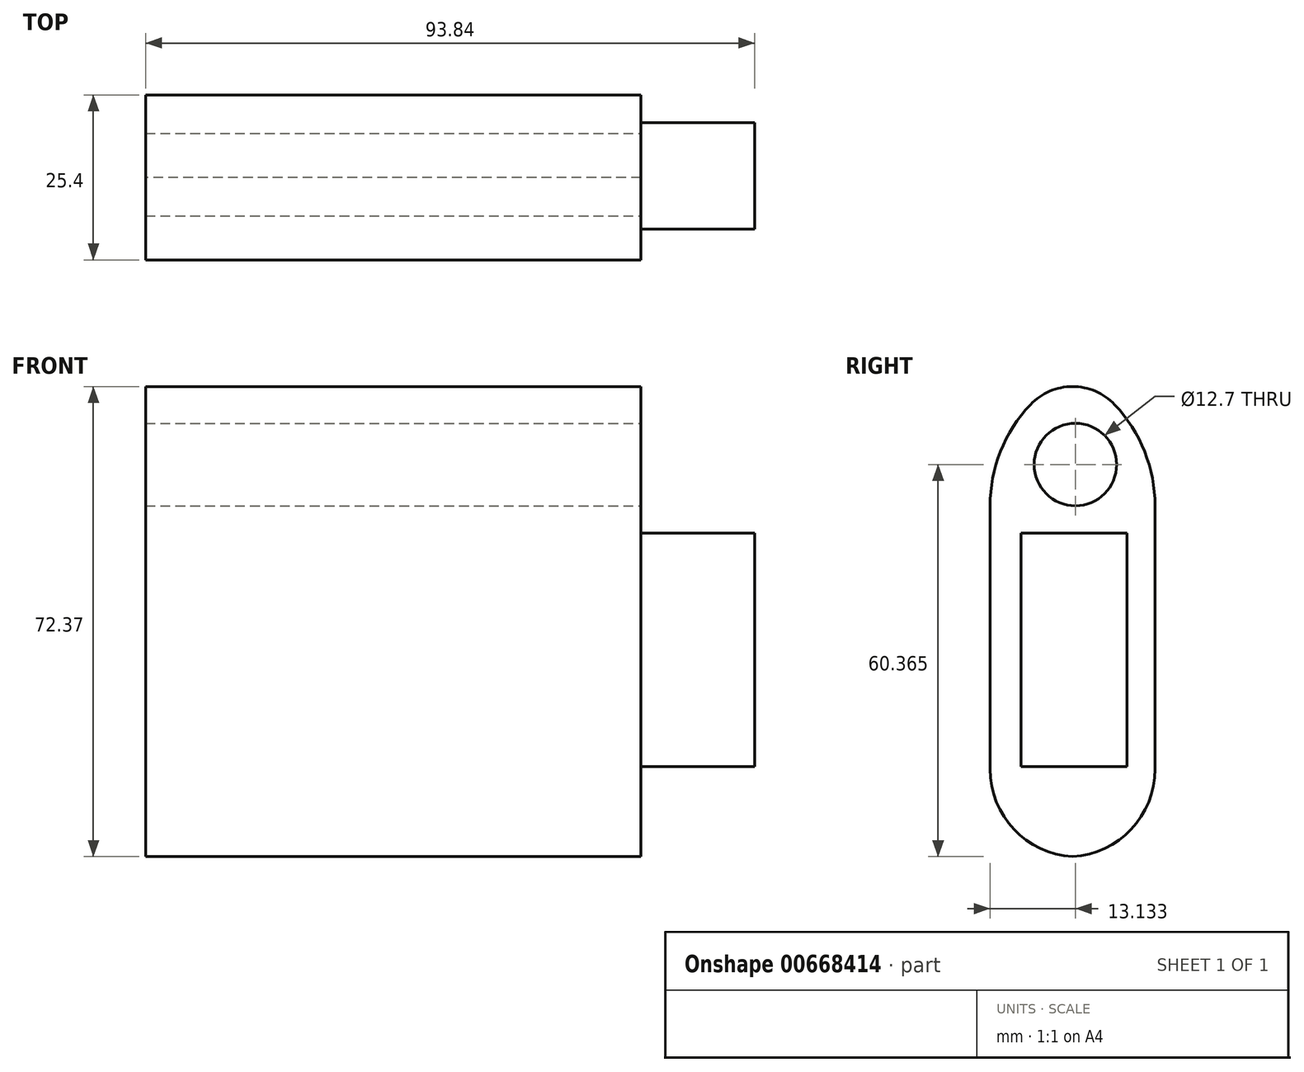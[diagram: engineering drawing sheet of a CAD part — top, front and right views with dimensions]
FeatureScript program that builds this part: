
annotation { "Feature Type Name" : "Feature", "Feature Type Description" : "" }
export const myFeature = defineFeature(function(context is Context, id is Id, definition is map)
    precondition{}
    {
        {
            var Q0;
            Q0=qCreatedBy(makeId("Front.planeOp"),FACE);
            var sketch = newSketch(context, id + "F0", { "sketchPlane" : qUnion([Q0])});
            skLineSegment(sketch, "E0.bottom", {"start": v(0, 0) * mm, "end": v(76.31, 0) * mm});
            skLineSegment(sketch, "E0.top", {"start": v(0, -76.7) * mm, "end": v(76.31, -76.7) * mm});
            skLineSegment(sketch, "E0.left", {"start": v(0, 0) * mm, "end": v(0, -76.7) * mm});
            skLineSegment(sketch, "E0.right", {"start": v(76.31, 0) * mm, "end": v(76.31, -76.7) * mm});
            skSolve(sketch);
        }
        {
            var Q0;
            Q0=makeQuery(id+"F0.imprint","IMPRINT",FACE,{"disambiguationData":[TD([[makeQuery(id+"F0.imprint","IMPRINT",EDGE,{"derivedFrom":sQuery(id+"F0.wireOp",EDGE,"E0.bottom")}),-1.0]])]});
            extrude(context, id + "F1", {"entities" : qUnion([Q0]), "depth" : 25.4 * mm, "offsetDistance" : 25.4 * mm});
        }
        {
            var Q0;
            Q0=makeQuery(id+"F1.opExtrude","CAP_EDGE",EDGE,{"disambiguationData":[OSD([sQuery(id+"F0.wireOp",EDGE,"E0.bottom")])],"isStart":false});
            var Q1;
            Q1=makeQuery(id+"F1.opExtrude","CAP_EDGE",EDGE,{"disambiguationData":[OSD([sQuery(id+"F0.wireOp",EDGE,"E0.bottom")])],"isStart":true});
            fillet(context, id + "F2", {"entities" : qUnion([Q0, Q1]), "radius" : 22.7 * mm, "tangentPropagation" : true, "allowEdgeOverflow" : false});
        }
        {
            var Q0;
            Q0=makeQuery(id+"F1.opExtrude","CAP_EDGE",EDGE,{"disambiguationData":[OSD([sQuery(id+"F0.wireOp",EDGE,"E0.top")])],"isStart":false});
            var Q1;
            Q1=makeQuery(id+"F1.opExtrude","CAP_EDGE",EDGE,{"disambiguationData":[OSD([sQuery(id+"F0.wireOp",EDGE,"E0.top")])],"isStart":true});
            fillet(context, id + "F3", {"entities" : qUnion([Q0, Q1]), "radius" : 13.5 * mm, "tangentPropagation" : true, "allowEdgeOverflow" : false});
        }
        {
            var Q0;
            {var subQ0=sQuery(id+"F0.wireOp",EDGE,"E0.bottom");Q0=makeQuery(id+"F2.opFillet","BLEND_EDGE",EDGE,{"blendedFrom":[makeQuery(id+"F1.opExtrude","CAP_EDGE",EDGE,{"disambiguationData":[OSD([subQ0])],"isStart":true}),makeQuery(id+"F1.opExtrude","CAP_EDGE",EDGE,{"disambiguationData":[OSD([subQ0])],"isStart":false})],"blendedInto":[]});}
            fillet(context, id + "F4", {"entities" : qUnion([Q0]), "radius" : 8.93 * mm, "tangentPropagation" : true, "allowEdgeOverflow" : false});
        }
        {
            var Q0;
            Q0=makeQuery(id+"F1.opExtrude","SWEPT_FACE",FACE,{"disambiguationData":[OSD([sQuery(id+"F0.wireOp",EDGE,"E0.right")])]});
            var sketch = newSketch(context, id + "F5", { "sketchPlane" : qUnion([Q0])});
            skCircle(sketch, "E1", {"center": v(-12.27, -16.3) * mm, "radius": 7.6 * mm});
            skSolve(sketch);
        }
        {
            var Q0;
            Q0=sQuery(id+"F5.wireOp",VERTEX,"E1.center");
            var Q1;
            Q1=makeQuery(id+"F1.opExtrude","SWEPT_BODY",BODY,{"disambiguationData":[OSD([sQuery(id+"F0.wireOp",EDGE,"E0.bottom"),sQuery(id+"F0.wireOp",EDGE,"E0.top"),sQuery(id+"F0.wireOp",EDGE,"E0.left"),sQuery(id+"F0.wireOp",EDGE,"E0.right")])]});
            hole(context, id + "F6", {"style" : HoleStyle.SIMPLE, "endStyle" : HoleEndStyle.THROUGH, "holeDiameter" : 12.7 * mm, "majorDiameter" : 6.35 * mm, "isTappedThrough" : true, "tappedDepth" : 12.7 * mm, "tapClearance" : 3, "locations" : qUnion([Q0]), "scope" : qUnion([Q1])});
        }
        {
            var Q0;
            Q0=makeQuery(id+"F1.opExtrude","SWEPT_FACE",FACE,{"disambiguationData":[OSD([sQuery(id+"F0.wireOp",EDGE,"E0.right")])]});
            var sketch = newSketch(context, id + "F7", { "sketchPlane" : qUnion([Q0])});
            skLineSegment(sketch, "E2.bottom", {"start": v(-20.66, -26.86) * mm, "end": v(-4.29, -26.86) * mm});
            skLineSegment(sketch, "E2.top", {"start": v(-20.66, -62.81) * mm, "end": v(-4.29, -62.81) * mm});
            skLineSegment(sketch, "E2.left", {"start": v(-20.66, -26.86) * mm, "end": v(-20.66, -62.81) * mm});
            skLineSegment(sketch, "E2.right", {"start": v(-4.29, -26.86) * mm, "end": v(-4.29, -62.81) * mm});
            skSolve(sketch);
        }
        {
            var Q0;
            Q0=makeQuery(id+"F7.imprint","IMPRINT",FACE,{"disambiguationData":[TD([[makeQuery(id+"F7.imprint","IMPRINT",EDGE,{"derivedFrom":sQuery(id+"F7.wireOp",EDGE,"E2.bottom")}),-1.0]])]});
            extrude(context, id + "F8", {"entities" : qUnion([Q0]), "operationType" : NewBodyOperationType.ADD, "depth" : 17.53 * mm, "offsetDistance" : 25.4 * mm});
        }
    });
